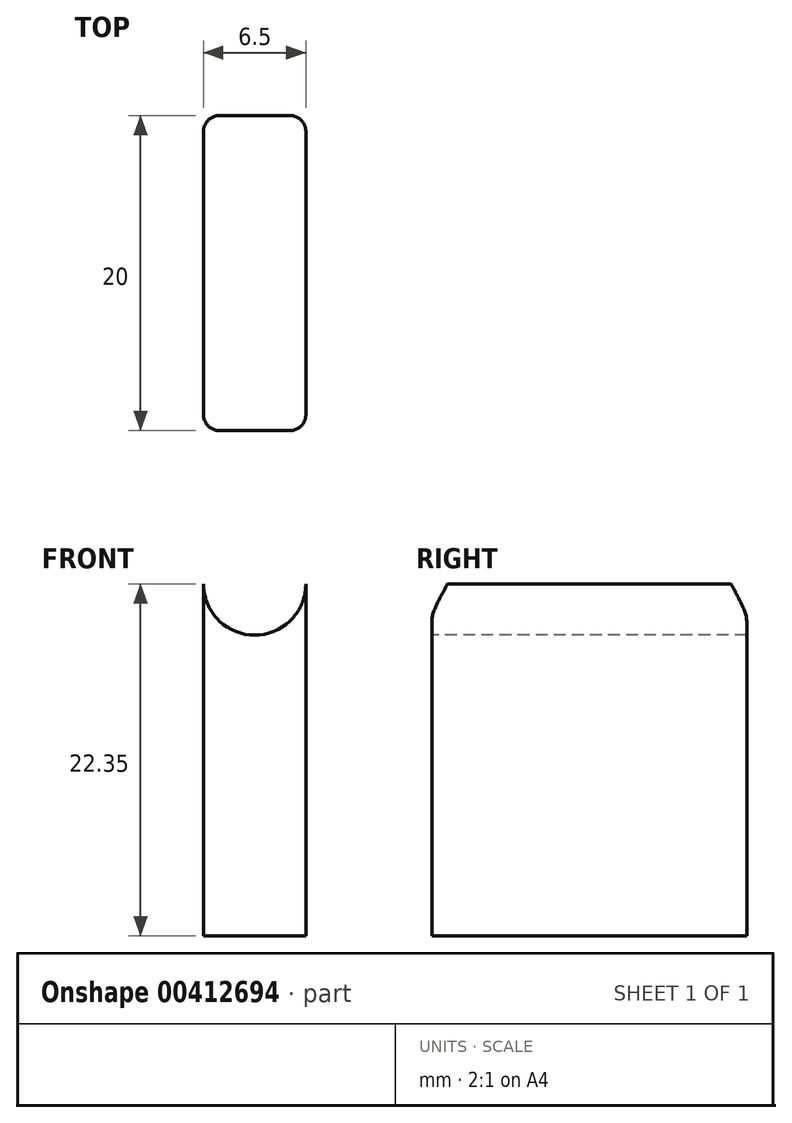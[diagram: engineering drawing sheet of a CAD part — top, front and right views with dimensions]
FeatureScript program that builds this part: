
annotation { "Feature Type Name" : "Feature", "Feature Type Description" : "" }
export const myFeature = defineFeature(function(context is Context, id is Id, definition is map)
    precondition{}
    {
        {
            var Q0;
            Q0=qCreatedBy(makeId("Top.planeOp"),FACE);
            var sketch = newSketch(context, id + "F0", { "sketchPlane" : qUnion([Q0])});
            skLineSegment(sketch, "E0.bottom", {"start": v(0, 0) * mm, "end": v(6.5, 0) * mm});
            skLineSegment(sketch, "E0.top", {"start": v(0, 20) * mm, "end": v(6.5, 20) * mm});
            skLineSegment(sketch, "E0.left", {"start": v(0, 0) * mm, "end": v(0, 20) * mm});
            skLineSegment(sketch, "E0.right", {"start": v(6.5, 0) * mm, "end": v(6.5, 20) * mm});
            skSolve(sketch);
        }
        {
            var Q0;
            Q0=makeQuery(id+"F0.imprint","IMPRINT",FACE,{"disambiguationData":[TD([[makeQuery(id+"F0.imprint","IMPRINT",EDGE,{"derivedFrom":sQuery(id+"F0.wireOp",EDGE,"E0.bottom")}),1.0]])]});
            extrude(context, id + "F1", {"entities" : qUnion([Q0]), "depth" : 22.35 * mm});
        }
        {
            var Q0;
            Q0=makeQuery(id+"F1.opExtrude","SWEPT_FACE",FACE,{"disambiguationData":[OSD([sQuery(id+"F0.wireOp",EDGE,"E0.bottom")])]});
            var sketch = newSketch(context, id + "F2", { "sketchPlane" : qUnion([Q0])});
            skLineSegment(sketch, "E1.0", {"start": v(0, 22.35) * mm, "end": v(6.5, 22.35) * mm});
            skCircle(sketch, "E2", {"center": v(3.25, 22.35) * mm, "radius": 3.25 * mm});
            skSolve(sketch);
        }
        {
            var Q0;
            Q0=qSketchRegion(id+"F2",true);
            extrude(context, id + "F3", {"entities" : qUnion([Q0]), "operationType" : NewBodyOperationType.REMOVE, "oppositeDirection" : true, "depth" : 25 * mm});
        }
        {
            var Q0;
            Q0=makeQuery(id+"F1.opExtrude","SWEPT_EDGE",EDGE,{"disambiguationData":[OSD([sQuery(id+"F0.wireOp",EDGE,"E0.bottom"),sQuery(id+"F0.wireOp",EDGE,"E0.right")])]});
            var Q1;
            Q1=makeQuery(id+"F1.opExtrude","SWEPT_EDGE",EDGE,{"disambiguationData":[OSD([sQuery(id+"F0.wireOp",EDGE,"E0.bottom"),sQuery(id+"F0.wireOp",EDGE,"E0.left")])]});
            var Q2;
            Q2=makeQuery(id+"F1.opExtrude","SWEPT_EDGE",EDGE,{"disambiguationData":[OSD([sQuery(id+"F0.wireOp",EDGE,"E0.top"),sQuery(id+"F0.wireOp",EDGE,"E0.right")])]});
            var Q3;
            Q3=makeQuery(id+"F1.opExtrude","SWEPT_EDGE",EDGE,{"disambiguationData":[OSD([sQuery(id+"F0.wireOp",EDGE,"E0.top"),sQuery(id+"F0.wireOp",EDGE,"E0.left")])]});
            fillet(context, id + "F4", {"entities" : qUnion([Q0, Q1, Q2, Q3]), "radius" : 1 * mm, "tangentPropagation" : true, "allowEdgeOverflow" : false});
        }
    });
